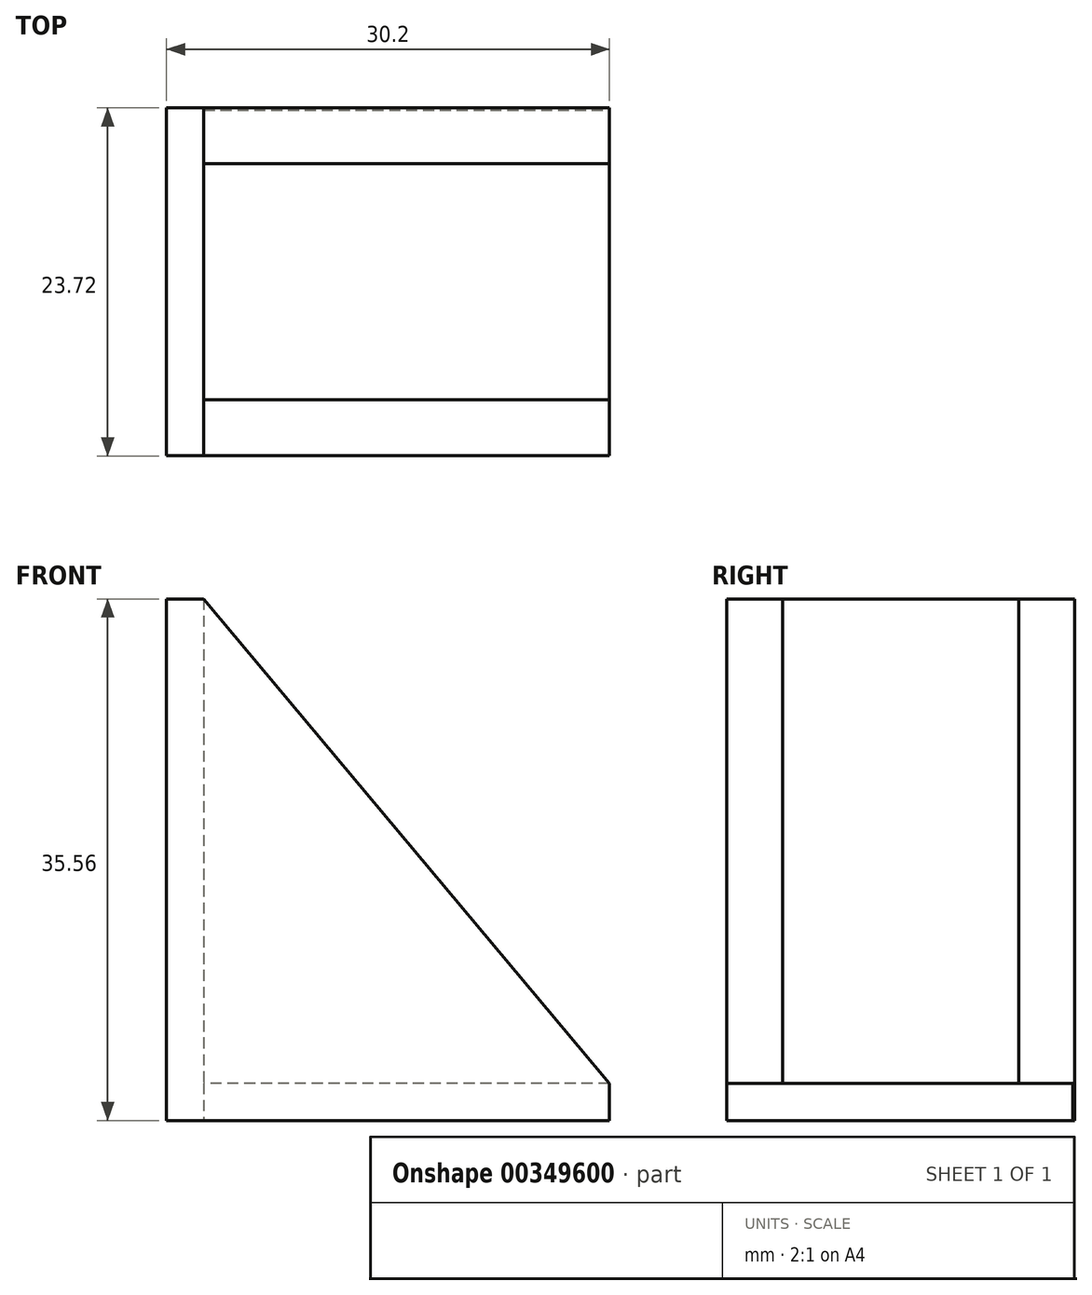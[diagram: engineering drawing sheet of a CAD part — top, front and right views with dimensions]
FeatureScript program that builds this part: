
annotation { "Feature Type Name" : "Feature", "Feature Type Description" : "" }
export const myFeature = defineFeature(function(context is Context, id is Id, definition is map)
    precondition{}
    {
        {
            var Q0;
            Q0=qCreatedBy(makeId("Top.planeOp"),FACE);
            var sketch = newSketch(context, id + "F0", { "sketchPlane" : qUnion([Q0])});
            skLineSegment(sketch, "E0.bottom", {"start": v(-27.66, 12.11) * mm, "end": v(0, 12.11) * mm});
            skLineSegment(sketch, "E0.top", {"start": v(-27.66, -11.46) * mm, "end": v(0, -11.46) * mm});
            skLineSegment(sketch, "E0.left", {"start": v(-27.66, 12.11) * mm, "end": v(-27.66, -11.46) * mm});
            skLineSegment(sketch, "E0.right", {"start": v(0, 12.11) * mm, "end": v(0, -11.46) * mm});
            skLineSegment(sketch, "E1.bottom", {"start": v(0, -11.46) * mm, "end": v(2.54, -11.46) * mm});
            skLineSegment(sketch, "E1.top", {"start": v(0, 12.26) * mm, "end": v(2.54, 12.26) * mm});
            skLineSegment(sketch, "E1.left", {"start": v(0, -11.46) * mm, "end": v(0, 12.26) * mm});
            skLineSegment(sketch, "E1.right", {"start": v(2.54, -11.46) * mm, "end": v(2.54, 12.26) * mm});
            skSolve(sketch);
        }
        {
            var Q0;
            {var subQ3=sQuery(id+"F0.wireOp",EDGE,"E1.bottom");Q0=makeQuery(id+"F0.imprint","IMPRINT",FACE,{"disambiguationData":[TD([[makeQuery(id+"F0.imprint","IMPRINT",EDGE,{"derivedFrom":subQ3}),1.0]])]});}
            extrude(context, id + "F1", {"entities" : qUnion([Q0]), "depth" : 35.56 * mm, "offsetDistance" : 25.4 * mm});
        }
        {
            var Q0;
            Q0=qCreatedBy(makeId("Top.planeOp"),FACE);
            var sketch = newSketch(context, id + "F2", { "sketchPlane" : qUnion([Q0])});
            skLineSegment(sketch, "E2.bottom", {"start": v(2.34, -11.59) * mm, "end": v(30, -11.59) * mm});
            skLineSegment(sketch, "E2.top", {"start": v(2.34, 11.98) * mm, "end": v(30, 11.98) * mm});
            skLineSegment(sketch, "E2.left", {"start": v(2.34, -11.59) * mm, "end": v(2.34, 11.98) * mm});
            skLineSegment(sketch, "E2.right", {"start": v(30, -11.59) * mm, "end": v(30, 11.98) * mm});
            skSolve(sketch);
        }
        {
            var Q0;
            Q0=makeQuery(id+"F1.opExtrude","SWEPT_BODY",BODY,{"disambiguationData":[OSD([sQuery(id+"F0.wireOp",EDGE,"E1.bottom"),sQuery(id+"F0.wireOp",EDGE,"E1.top"),sQuery(id+"F0.wireOp",EDGE,"E1.left"),sQuery(id+"F0.wireOp",EDGE,"E1.right")])]});
            var Q1;
            Q1=makeQuery(id+"F1.opExtrude","CAP_VERTEX",VERTEX,{"disambiguationData":[OSD([sQuery(id+"F0.wireOp",EDGE,"E1.bottom"),sQuery(id+"F0.wireOp",EDGE,"E1.right")])],"isStart":true});
            var Q2;
            Q2=sQuery(id+"F2.wireOp",VERTEX,"E2.left.start");
            transform(context, id + "F3", {"entities" : qUnion([Q0]), "transformType" : TransformType.TRANSLATION_ENTITY, "oppositeDirectionEntity" : false, "transformLine" : qUnion([Q1, Q2]), "makeCopy" : false});
        }
        {
            var Q0;
            Q0 = qSketchRegion(id + "F2", true);
            extrude(context, id + "F4", {"entities" : qUnion([Q0]), "operationType" : NewBodyOperationType.ADD, "depth" : 2.54 * mm, "offsetDistance" : 25.4 * mm});
        }
        {
            var Q0;
            Q0=makeQuery(id+"F4.boolean.opBoolean","MERGE",FACE,{"derivedFrom":[makeQuery(id+"F1.opExtrude","SWEPT_FACE",FACE,{"disambiguationData":[OSD([sQuery(id+"F0.wireOp",EDGE,"E1.bottom")])]}),makeQuery(id+"F4.opExtrude","SWEPT_FACE",FACE,{"disambiguationData":[OSD([sQuery(id+"F2.wireOp",EDGE,"E2.bottom")])]})]});
            var sketch = newSketch(context, id + "F5", { "sketchPlane" : qUnion([Q0])});
            skLineSegment(sketch, "E3", {"start": v(2.34, 35.56) * mm, "end": v(30, 2.54) * mm});
            skSolve(sketch);
        }
        {
            var Q0;
            Q0=makeQuery(id+"F1.opExtrude","SWEPT_FACE",FACE,{"disambiguationData":[OSD([sQuery(id+"F0.wireOp",EDGE,"E1.top")])]});
            var sketch = newSketch(context, id + "F6", { "sketchPlane" : qUnion([Q0])});
            skPoint(sketch, "E4", {"position": v(-30, 2.54) * mm});
            skLineSegment(sketch, "E5", {"start": v(-30, 2.54) * mm, "end": v(-2.34, 35.56) * mm});
            skPoint(sketch, "E6", {"position": v(-2.34, 2.54) * mm});
            skLineSegment(sketch, "E7", {"start": v(-2.34, 35.56) * mm, "end": v(-2.34, 2.54) * mm});
            skLineSegment(sketch, "E8", {"start": v(-30, 2.54) * mm, "end": v(-2.34, 2.54) * mm});
            skSolve(sketch);
        }
        {
            var Q0;
            Q0=makeQuery(id+"F5.imprint","IMPRINT",FACE,{"disambiguationData":[TD([[makeQuery(id+"F5.imprint","IMPRINT",EDGE,{"derivedFrom":sQuery(id+"F5.wireOp",EDGE,"E3")}),-1.0]])]});
            extrude(context, id + "F7", {"entities" : qUnion([Q0]), "operationType" : NewBodyOperationType.ADD, "oppositeDirection" : true, "depth" : 3.8 * mm, "offsetDistance" : 25.4 * mm});
        }
        {
            var Q0;
            Q0=makeQuery(id+"F6.imprint","IMPRINT",FACE,{"disambiguationData":[TD([[makeQuery(id+"F6.imprint","IMPRINT",EDGE,{"derivedFrom":sQuery(id+"F6.wireOp",EDGE,"E5")}),-1.0]])]});
            extrude(context, id + "F8", {"entities" : qUnion([Q0]), "operationType" : NewBodyOperationType.ADD, "oppositeDirection" : true, "depth" : 3.8 * mm, "offsetDistance" : 25.4 * mm});
        }
    });
